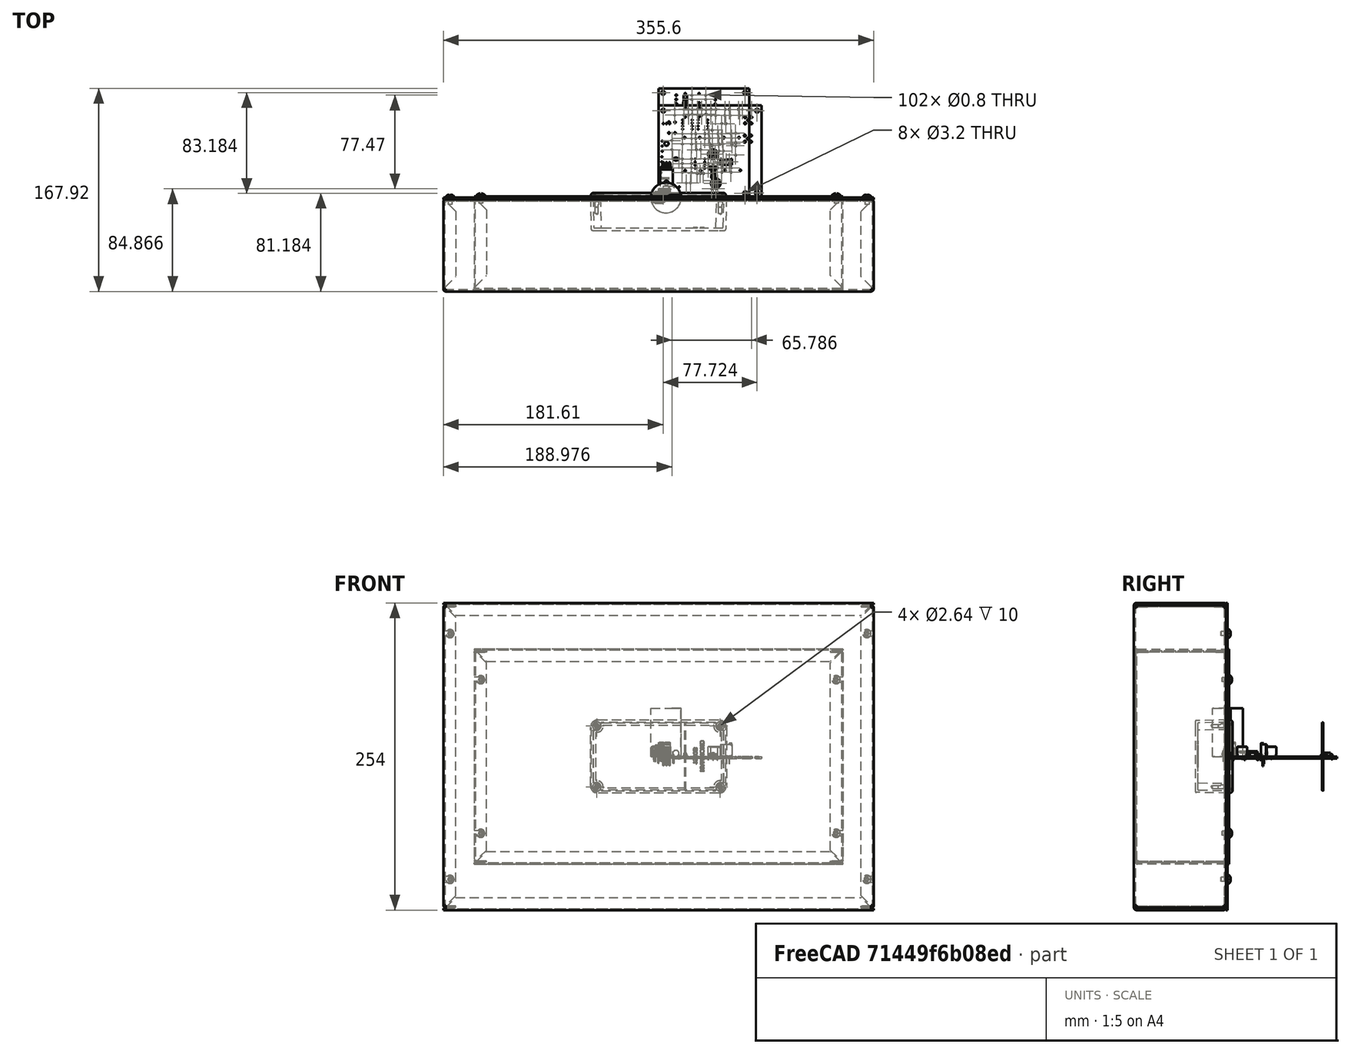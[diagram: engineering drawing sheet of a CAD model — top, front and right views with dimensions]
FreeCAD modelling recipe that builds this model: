
FCSTD DOCUMENT  (FreeCAD 0.20R29603 (Git))
Label: hammond-enclosure
License: All rights reserved
LicenseURL: http://en.wikipedia.org/wiki/All_rights_reserved
objects: Part::Feature×77, App::Link×60, App::Part×20, PartDesign::CoordinateSystem×2, Sketcher::SketchObject×2
note: 81 computed .brp shape members not serialized (recipe doc carries the construction recipe); baked Part::Feature solids carry a one-line shape summary decoded from their .brp

FEATURE [Part::Feature] Part__Feature  label="1444-1273"
  Placement = pos=(0,-76.2,1.8e-14) rot=(0.57735,0.57735,0.57735;4.18879rad)
  shape: bbox 304.8 x 76.2 x 177.8 mm, 114 faces (baked)
FEATURE [Part::Feature] Part__Feature001  label="1434-127"
  shape: bbox 304.8 x 1.016 x 177.8 mm, 26 faces (baked)
FEATURE [Part::Feature] Part__Feature002  label="6-32 (SC18394)"
  Placement = pos=(146.863,-0.508,63.5) rot=(0,0,1;0rad)
  shape: bbox 7.29 x 8.224 x 7.29 mm, 27 faces (baked)
FEATURE [Part::Feature] Part__Feature003  label="6-32 (SC18394)001"
  Placement = pos=(146.863,-0.508,-63.5) rot=(0,0,1;0rad)
  shape: bbox 7.29 x 8.224 x 7.29 mm, 27 faces (baked)
FEATURE [Part::Feature] Part__Feature004  label="6-32 (SC18394)002"
  Placement = pos=(-146.863,-0.508,-63.5) rot=(0,0,1;0rad)
  shape: bbox 7.29 x 8.224 x 7.29 mm, 27 faces (baked)
FEATURE [Part::Feature] Part__Feature005  label="6-32 (SC18394)003"
  Placement = pos=(-146.863,-0.508,63.5) rot=(0,0,1;0rad)
  shape: bbox 7.29 x 8.224 x 7.29 mm, 27 faces (baked)
FEATURE [App::Part] _444_1273  label="1444-1274"
  Group = -> [Part__Feature,Part__Feature001,Part__Feature002,Part__Feature003,Part__Feature004,Part__Feature005]
  Origin = -> Origin
FEATURE [Part::Feature] Part__Feature006  label="1590B BOX"
  Placement = pos=(0,0,0) rot=(-1,0,0;1.5708rad)
  shape: bbox 112.4 x 261 x 60.52 mm, 255 faces (baked)
FEATURE [Part::Feature] Part__Feature007  label="1590B-BS LID"
  Placement = pos=(0,0,0) rot=(0,0.707107,-0.707107;3.14159rad)
  shape: bbox 112.4 x 6.014 x 61.03 mm, 68 faces (baked)
FEATURE [Part::Feature] Part__Feature008  label="SC530 (screw #6-32X 1_2' FH)"
  Placement = pos=(-51.05,1.5362,25.25) rot=(0,1,0;0.650238rad)
  shape: bbox 6.871 x 11.85 x 6.871 mm, 25 faces (baked)
FEATURE [Part::Feature] Part__Feature009  label="SC530 (screw #6-32X 1_2' FH)001"
  Placement = pos=(-51.05,1.5362,-25.25) rot=(0,-1,0;0.529817rad)
  shape: bbox 6.871 x 11.85 x 6.871 mm, 25 faces (baked)
FEATURE [Part::Feature] Part__Feature010  label="SC530 (screw #6-32X 1_2' FH)002"
  Placement = pos=(51.05,1.5362,25.25) rot=(0,0,1;0rad)
  shape: bbox 6.871 x 11.85 x 6.871 mm, 25 faces (baked)
FEATURE [Part::Feature] Part__Feature011  label="SC530 (screw #6-32X 1_2' FH)003"
  Placement = pos=(51.05,1.5362,-25.25) rot=(0,0,1;0rad)
  shape: bbox 6.871 x 11.85 x 6.871 mm, 25 faces (baked)
FEATURE [App::Part] _590B  label="1590B-1"
  Group = -> [Part__Feature006,Part__Feature007,Part__Feature008,Part__Feature009,Part__Feature010,Part__Feature011]
  Origin = -> Origin001
  Placement = pos=(-86,-43,49) rot=(0,0,1;0rad)
FEATURE [Part::Feature] Part__Feature012  label="1590B BOX001"
  Placement = pos=(0,0,0) rot=(-1,0,0;1.5708rad)
  shape: bbox 112.4 x 261 x 60.52 mm, 255 faces (baked)
FEATURE [Part::Feature] Part__Feature013  label="1590B-BS LID001"
  Placement = pos=(0,0,0) rot=(0,0.707107,-0.707107;3.14159rad)
  shape: bbox 112.4 x 6.014 x 61.03 mm, 68 faces (baked)
FEATURE [Part::Feature] Part__Feature014  label="SC530 (screw #6-32X 1_2' FH)004"
  Placement = pos=(-51.05,1.5362,25.25) rot=(0,1,0;0.650238rad)
  shape: bbox 6.871 x 11.85 x 6.871 mm, 25 faces (baked)
FEATURE [Part::Feature] Part__Feature015  label="SC530 (screw #6-32X 1_2' FH)005"
  Placement = pos=(-51.05,1.5362,-25.25) rot=(0,-1,0;0.529817rad)
  shape: bbox 6.871 x 11.85 x 6.871 mm, 25 faces (baked)
FEATURE [Part::Feature] Part__Feature016  label="SC530 (screw #6-32X 1_2' FH)006"
  Placement = pos=(51.05,1.5362,25.25) rot=(0,0,1;0rad)
  shape: bbox 6.871 x 11.85 x 6.871 mm, 25 faces (baked)
FEATURE [Part::Feature] Part__Feature017  label="SC530 (screw #6-32X 1_2' FH)007"
  Placement = pos=(51.05,1.5362,-25.25) rot=(0,0,1;0rad)
  shape: bbox 6.871 x 11.85 x 6.871 mm, 25 faces (baked)
FEATURE [App::Part] _590B001  label="1590B-2"
  Group = -> [Part__Feature012,Part__Feature013,Part__Feature014,Part__Feature015,Part__Feature016,Part__Feature017]
  Origin = -> Origin002
  Placement = pos=(-84,-43,-16) rot=(0,0,1;0rad)
FEATURE [Part::Feature] Part__Feature018  label="1590B BOX002"
  Placement = pos=(0,0,0) rot=(-1,0,0;1.5708rad)
  shape: bbox 112.4 x 261 x 60.52 mm, 255 faces (baked)
FEATURE [Part::Feature] Part__Feature019  label="1590B-BS LID002"
  Placement = pos=(0,0,0) rot=(0,0.707107,-0.707107;3.14159rad)
  shape: bbox 112.4 x 6.014 x 61.03 mm, 68 faces (baked)
FEATURE [Part::Feature] Part__Feature020  label="SC530 (screw #6-32X 1_2' FH)008"
  Placement = pos=(-51.05,1.5362,25.25) rot=(0,1,0;0.650238rad)
  shape: bbox 6.871 x 11.85 x 6.871 mm, 25 faces (baked)
FEATURE [Part::Feature] Part__Feature021  label="SC530 (screw #6-32X 1_2' FH)009"
  Placement = pos=(-51.05,1.5362,-25.25) rot=(0,-1,0;0.529817rad)
  shape: bbox 6.871 x 11.85 x 6.871 mm, 25 faces (baked)
FEATURE [Part::Feature] Part__Feature022  label="SC530 (screw #6-32X 1_2' FH)010"
  Placement = pos=(51.05,1.5362,25.25) rot=(0,0,1;0rad)
  shape: bbox 6.871 x 11.85 x 6.871 mm, 25 faces (baked)
FEATURE [Part::Feature] Part__Feature023  label="SC530 (screw #6-32X 1_2' FH)011"
  Placement = pos=(51.05,1.5362,-25.25) rot=(0,0,1;0rad)
  shape: bbox 6.871 x 11.85 x 6.871 mm, 25 faces (baked)
FEATURE [App::Part] _590B002  label="1590B-3"
  Group = -> [Part__Feature018,Part__Feature019,Part__Feature020,Part__Feature021,Part__Feature022,Part__Feature023]
  Origin = -> Origin003
  Placement = pos=(-85,-9,49) rot=(0,0,1;0rad)
FEATURE [PartDesign::CoordinateSystem] Local_CS_7b02
  AttacherType = Attacher::AttachEngine3D
  MapMode = 2
  Support = -> [X_Axis005]
FEATURE [Part::Feature] Pcb_7b02
  Placement = pos=(-75.946,138.684,0) rot=(0,0,1;0rad)
  shape: bbox 75.18 x 90.42 x 1.6 mm, 56 faces (baked)
FEATURE [Sketcher::SketchObject] PCB_Sketch_7b02
  FullyConstrained = false
  sketch-geometry (4):
    g0: LineSegment StartX=0 StartY=90.424 StartZ=0 EndX=75.184 EndY=90.424 EndZ=0
    g1: LineSegment StartX=75.184 StartY=90.424 StartZ=0 EndX=75.184 EndY=0 EndZ=0
    g2: LineSegment StartX=75.184 StartY=0 StartZ=0 EndX=0 EndY=0 EndZ=0
    g3: LineSegment StartX=0 StartY=0 StartZ=0 EndX=0 EndY=90.424 EndZ=0
  constraints (4):
    c: Coincident(g2,g3)
    c: Coincident(g0,g3)
    c: Coincident(g1,g2)
    c: Coincident(g0,g1)
FEATURE [App::Part] Board_Geoms_7b02
  Group = -> [Pcb_7b02,PCB_Sketch_7b02]
  Origin = -> Origin004
FEATURE [Part::Feature] Part__Feature024  label="part"
  shape: bbox 0.508 x 0.508 x 4.064 mm, 3 faces (baked)
FEATURE [Part::Feature] Part__Feature025  label="part001"
  shape: bbox 0.508 x 0.508 x 4.064 mm, 3 faces (baked)
FEATURE [Part::Feature] Part__Feature026  label="part002"
  shape: bbox 5.994 x 3.506 x 8.509 mm, 6 faces (baked)
FEATURE [App::Part] part  label="C909_part003_af03f52f8d81"
  Group = -> [Part__Feature024,Part__Feature025,Part__Feature026]
  Origin = -> Origin012
  Placement = pos=(39.37,72.644,0) rot=(0,0,-1;1.5708rad)
FEATURE [App::Link] C909_part003_af03f52f8d81_ln_  label="C906_part003_3db3d25175d7"
  LinkPlacement = pos=(27.691,84.808,0) rot=(0,0,-1;1.5708rad)
  LinkedObject = -> part
  Placement = pos=(27.691,84.808,0) rot=(0,0,-1;1.5708rad)
FEATURE [Part::Feature] Part__Feature027  label="SOLID"
  Placement = pos=(0,0,4.2) rot=(0,0,1;0rad)
  shape: bbox 2.75 x 3.75 x 8.15 mm, 17 faces (baked)
FEATURE [Part::Feature] Part__Feature028  label="SOLID001"
  Placement = pos=(0,0,4.2) rot=(0,0,1;0rad)
  shape: bbox 2.75 x 3.75 x 8.15 mm, 17 faces (baked)
FEATURE [Part::Feature] Part__Feature029  label="SOLID002"
  Placement = pos=(0,0,4.2) rot=(0,0,1;0rad)
  shape: bbox 2.75 x 3.75 x 8.15 mm, 17 faces (baked)
FEATURE [Part::Feature] Part__Feature030  label="SOLID003"
  Placement = pos=(0,0,4.2) rot=(0,0,1;0rad)
  shape: bbox 2.9 x 4.5 x 2.65 mm, 46 faces (baked)
FEATURE [Part::Feature] Part__Feature031  label="SOLID004"
  Placement = pos=(0,0,4.2) rot=(0,0,1;0rad)
  shape: bbox 2.9 x 4.5 x 2.65 mm, 46 faces (baked)
FEATURE [Part::Feature] Part__Feature032  label="SOLID005"
  Placement = pos=(0,0,4.2) rot=(0,0,1;0rad)
  shape: bbox 2.9 x 4.5 x 2.65 mm, 46 faces (baked)
FEATURE [Part::Feature] Part__Feature033  label="SOLID006"
  Placement = pos=(0,0,4.2) rot=(0,0,1;0rad)
  shape: bbox 3.139 x 3.139 x 4.6 mm, 17 faces (baked)
FEATURE [Part::Feature] Part__Feature034  label="SOLID007"
  Placement = pos=(0,0,4.2) rot=(0,0,1;0rad)
  shape: bbox 3.139 x 3.139 x 4.6 mm, 17 faces (baked)
FEATURE [Part::Feature] Part__Feature035  label="SOLID008"
  Placement = pos=(0,0,4.2) rot=(0,0,1;0rad)
  shape: bbox 3.139 x 3.139 x 4.6 mm, 17 faces (baked)
FEATURE [Part::Feature] Part__Feature036  label="SOLID009"
  Placement = pos=(0,0,4.2) rot=(0,0,1;0rad)
  shape: bbox 11.5 x 7 x 8.4 mm, 98 faces (baked)
FEATURE [App::Part] _91103110003_1  label="J901_691103110003_1_4d612100a2a6"
  Group = -> [Part__Feature027,Part__Feature028,Part__Feature029,Part__Feature030,Part__Feature031,Part__Feature032,Part__Feature033,Part__Feature034,Part__Feature035,Part__Feature036]
  Origin = -> Origin013
  Placement = pos=(14.732,81.28,0) rot=(0,0,-1;1.5708rad)
FEATURE [App::Link] J901_691103110003_1_4d612100a2a6_ln_  label="J901_691103110003_1_4d612100a2a6[2]"
  LinkPlacement = pos=(14.732,81.28,4) rot=(0,0,-1;1.5708rad)
  LinkedObject = -> _91103110003_1
  Placement = pos=(14.732,81.28,4) rot=(0,0,-1;1.5708rad)
FEATURE [Part::Feature] Shape  label="D901_D_DO-41_SOD81_P7.62mm_Horizontal_0f7420698e15"
  Placement = pos=(22.098,78.486,0) rot=(0,0,1;1.5708rad)
  shape: bbox 2.72 x 8.618 x 5.71 mm, 15 faces (baked)
FEATURE [Part::Feature] Shape001  label="D901_SOD57  BYT62-BY203_6-563-5006-5-4_0f7420698e15[2]"
  Placement = pos=(22.098,78.486,0) rot=(0,0,1;1.5708rad)
  shape: bbox 4.349 x 4.349 x 56.22 mm, 10 faces (baked)
FEATURE [App::Link] D901_D_DO_41_SOD81_P7_62mm_Horizontal_0f7420698e15_ln_  label="D904_D_DO-41_SOD81_P7.62mm_Horizontal_3765f3f7798b"
  LinkPlacement = pos=(33.528,66.802,0) rot=(0,0,1;1.5708rad)
  LinkedObject = -> Shape
  Placement = pos=(33.528,66.802,0) rot=(0,0,1;1.5708rad)
FEATURE [Part::Feature] Part__Feature037  label="part003"
  shape: bbox 1.016 x 1.016 x 5.588 mm, 3 faces (baked)
FEATURE [Part::Feature] Part__Feature038  label="part004"
  shape: bbox 1.016 x 1.016 x 5.588 mm, 3 faces (baked)
FEATURE [Part::Feature] Part__Feature039  label="part005"
  shape: bbox 24.99 x 24.99 x 39.75 mm, 3 faces (baked)
FEATURE [Part::Feature] Part__Feature040  label="part006"
  shape: bbox 10.02 x 4.878 x 31.83 mm, 8 faces (baked)
FEATURE [App::Part] part001  label="C911_part007_10cb9a3285f4"
  Group = -> [Part__Feature037,Part__Feature038,Part__Feature039,Part__Feature040]
  Origin = -> Origin014
  Placement = pos=(54.102,49.784,0) rot=(0,0,1;0rad)
FEATURE [App::Link] C911_part007_10cb9a3285f4_ln_  label="C902_part007_474a571f78e2"
  LinkPlacement = pos=(21.59,49.784,0) rot=(0,0,1;0rad)
  LinkedObject = -> part001
  Placement = pos=(21.59,49.784,0) rot=(0,0,1;0rad)
FEATURE [Part::Feature] Shape002  label="R902_R_Axial_DIN0309_L90mm_D32mm_P1270mm_Horizontal_656395d6a1e4"
  Placement = pos=(45.212,14.224,0) rot=(0,0,1;1.5708rad)
  shape: bbox 3.464 x 13.63 x 6.332 mm, 17 faces (baked)
FEATURE [App::Link] C911_part007_10cb9a3285f4_ln_001  label="C910_part007_5ecea69d9437"
  LinkPlacement = pos=(55.118,22.606,0) rot=(0,0,1;0rad)
  LinkedObject = -> part001
  Placement = pos=(55.118,22.606,0) rot=(0,0,1;0rad)
FEATURE [App::Link] C909_part003_af03f52f8d81_ln_001  label="C907_part007_ae6a843ea56a"
  LinkPlacement = pos=(27.945,72.616,0) rot=(0,0,-1;1.5708rad)
  LinkedObject = -> part
  Placement = pos=(27.945,72.616,0) rot=(0,0,-1;1.5708rad)
FEATURE [Part::Feature] Shape003  label="C904_CP_Radial_D80mm_P350mm_be9362f17a2f"
  Placement = pos=(43.2449,36.068,0) rot=(0,0,1;0rad)
  shape: bbox 9.886 x 10.23 x 10 mm, 54 faces (baked)
FEATURE [App::Link] D901_D_DO_41_SOD81_P7_62mm_Horizontal_0f7420698e15_ln_001  label="D902_D_DO-41_SOD81_P7.62mm_Horizontal_acca8f042afe"
  LinkPlacement = pos=(22.098,66.802,0) rot=(0,0,1;1.5708rad)
  LinkedObject = -> Shape
  Placement = pos=(22.098,66.802,0) rot=(0,0,1;1.5708rad)
FEATURE [App::Link] C904_CP_Radial_D80mm_P350mm_be9362f17a2f_ln_  label="C905_CP_Radial_D80mm_P350mm_1a9500cd5eb0"
  LinkPlacement = pos=(44.0069,7.366,0) rot=(0,0,1;0rad)
  LinkedObject = -> Shape003
  Placement = pos=(44.0069,7.366,0) rot=(0,0,1;0rad)
FEATURE [App::Link] R902_R_Axial_DIN0309_L90mm_D32mm_P1270mm_Horizontal_656395d6a1e4_ln_  label="R901_R_Axial_DIN0309_L90mm_D32mm_P1270mm_Horizontal_c8b94c641cc7"
  LinkPlacement = pos=(44.45,43.18,0) rot=(0,0,1;1.5708rad)
  LinkedObject = -> Shape002
  Placement = pos=(44.45,43.18,0) rot=(0,0,1;1.5708rad)
FEATURE [Part::Feature] Shape004  label="U902_TO-220-3_Horizontal_TabUp_336c31f2f8c4"
  Placement = pos=(4.064,28.956,0) rot=(0,0,1;0rad)
  shape: bbox 10.25 x 19.74 x 12.59 mm, 80 faces (baked)
FEATURE [App::Link] U902_TO_220_3_Horizontal_TabUp_336c31f2f8c4_ln_  label="U902_TO-220-3_Horizontal_TabUp_336c31f2f8c4[2]"
  LinkPlacement = pos=(4.064,28.956,0) rot=(0,0,1;0rad)
  LinkedObject = -> Shape004
  Placement = pos=(4.064,28.956,0) rot=(0,0,1;0rad)
FEATURE [App::Link] J901_691103110003_1_4d612100a2a6_ln_001  label="J902_691103110003_1_2f685726ded9"
  LinkPlacement = pos=(46.99,81.026,0) rot=(0,0,1;1.5708rad)
  LinkedObject = -> _91103110003_1
  Placement = pos=(46.99,81.026,0) rot=(0,0,1;1.5708rad)
FEATURE [App::Link] J901_691103110003_1_4d612100a2a6_ln_002  label="J902_691103110003_1_2f685726ded9[2]"
  LinkPlacement = pos=(46.99,81.026,4) rot=(0,0,1;1.5708rad)
  LinkedObject = -> _91103110003_1
  Placement = pos=(46.99,81.026,4) rot=(0,0,1;1.5708rad)
FEATURE [App::Link] D901_D_DO_41_SOD81_P7_62mm_Horizontal_0f7420698e15_ln_002  label="D903_D_DO-41_SOD81_P7.62mm_Horizontal_fd54faef2eec"
  LinkPlacement = pos=(33.528,78.486,0) rot=(0,0,1;1.5708rad)
  LinkedObject = -> Shape
  Placement = pos=(33.528,78.486,0) rot=(0,0,1;1.5708rad)
FEATURE [App::Link] U902_TO_220_3_Horizontal_TabUp_336c31f2f8c4_ln_001  label="U901_TO-220-3_Horizontal_TabUp_2bf8607644b3"
  LinkPlacement = pos=(4.064,61.3,0) rot=(0,0,1;0rad)
  LinkedObject = -> Shape004
  Placement = pos=(4.064,61.3,0) rot=(0,0,1;0rad)
FEATURE [App::Link] U902_TO_220_3_Horizontal_TabUp_336c31f2f8c4_ln_002  label="U901_TO-220-3_Horizontal_TabUp_2bf8607644b3[2]"
  LinkPlacement = pos=(4.064,61.3,0) rot=(0,0,1;0rad)
  LinkedObject = -> Shape004
  Placement = pos=(4.064,61.3,0) rot=(0,0,1;0rad)
FEATURE [App::Link] C909_part003_af03f52f8d81_ln_002  label="C908_part007_641f8a291a63"
  LinkPlacement = pos=(39.121,84.836,0) rot=(0,0,-1;1.5708rad)
  LinkedObject = -> part
  Placement = pos=(39.121,84.836,0) rot=(0,0,-1;1.5708rad)
FEATURE [App::Link] C911_part007_10cb9a3285f4_ln_002  label="C903_part007_61d36386d3d2"
  LinkPlacement = pos=(22.1411,22.352,0) rot=(0,0,1;0rad)
  LinkedObject = -> part001
  Placement = pos=(22.1411,22.352,0) rot=(0,0,1;0rad)
FEATURE [App::Part] Top_7b02
  Group = -> [part,C909_part003_af03f52f8d81_ln_,_91103110003_1,J901_691103110003_1_4d612100a2a6_ln_,Shape,Shape001,D901_D_DO_41_SOD81_P7_62mm_Horizontal_0f7420698e15_ln_,part001,C911_part007_10cb9a3285f4_ln_,Shape002,C911_part007_10cb9a3285f4_ln_001,C909_part003_af03f52f8d81_ln_001,Shape003,D901_D_DO_41_SOD81_P7_62mm_Horizontal_0f7420698e15_ln_001,C904_CP_Radial_D80mm_P350mm_be9362f17a2f_ln_,+10 more]
  Origin = -> Origin007
FEATURE [App::Part] Step_Models_7b02
  Group = -> [Top_7b02]
  Origin = -> Origin006
FEATURE [App::Part] Board_7b02  label="15v-supply"
  Group = -> [Local_CS_7b02,Board_Geoms_7b02,Step_Models_7b02]
  Origin = -> Origin005
  Placement = pos=(62,-65,-77) rot=(0.57735,0.57735,0.57735;4.18879rad)
FEATURE [PartDesign::CoordinateSystem] Local_CS_758f
  AttacherType = Attacher::AttachEngine3D
  MapMode = 2
  Support = -> [X_Axis016]
FEATURE [Part::Feature] Pcb_758f
  Placement = pos=(-97.028,138.43,0) rot=(0,0,1;0rad)
  shape: bbox 85.34 x 76.45 x 1.6 mm, 146 faces (baked)
FEATURE [Sketcher::SketchObject] PCB_Sketch_758f
  FullyConstrained = false
  sketch-geometry (4):
    g0: LineSegment StartX=0 StartY=76.454 StartZ=0 EndX=85.344 EndY=76.454 EndZ=0
    g1: LineSegment StartX=85.344 StartY=76.454 StartZ=0 EndX=85.344 EndY=0 EndZ=0
    g2: LineSegment StartX=85.344 StartY=0 StartZ=0 EndX=0 EndY=0 EndZ=0
    g3: LineSegment StartX=0 StartY=0 StartZ=0 EndX=0 EndY=76.454 EndZ=0
  constraints (4):
    c: Coincident(g2,g3)
    c: Coincident(g0,g3)
    c: Coincident(g1,g2)
    c: Coincident(g0,g1)
FEATURE [App::Part] Board_Geoms_758f
  Group = -> [Pcb_758f,PCB_Sketch_758f]
  Origin = -> Origin015
FEATURE [Part::Feature] Shape005  label="R426_R_Axial_DIN0207_L63mm_D25mm_P762mm_Horizontal_96b38c16849e"
  Placement = pos=(48.768,24.638,0) rot=(0,0,1;3.14159rad)
  shape: bbox 8.418 x 2.706 x 5.603 mm, 15 faces (baked)
FEATURE [Part::Feature] Part__Feature041  label="D_DO-35_SOD27_P7.62mm_Horizontal"
  shape: bbox 8.244 x 0.5 x 4.312 mm, 7 faces (baked)
FEATURE [Part::Feature] Part__Feature042  label="D_DO-35_SOD27_P7.62mm_Horizontal001"
  shape: bbox 4 x 2.165 x 2.165 mm, 9 faces (baked)
FEATURE [App::Part] D_DO_35_SOD27_P7_62mm_Horizontal  label="D401_D_DO-35_SOD27_P7.62mm_Horizontal002_a58dadb01c92"
  Group = -> [Part__Feature041,Part__Feature042]
  Origin = -> Origin023
  Placement = pos=(24.638,73.152,0) rot=(0,0,1;0rad)
FEATURE [App::Link] R426_R_Axial_DIN0207_L63mm_D25mm_P762mm_Horizontal_96b38c16849e_ln_  label="R411_R_Axial_DIN0207_L63mm_D25mm_P762mm_Horizontal_dd1791483003"
  LinkPlacement = pos=(13.462,68.326,0) rot=(0,0,1;0rad)
  LinkedObject = -> Shape005
  Placement = pos=(13.462,68.326,0) rot=(0,0,1;0rad)
FEATURE [Part::Feature] Shape006  label="C405_CP_Radial_D80mm_P350mm_98bf3544fc31"
  Placement = pos=(45.5913,11.938,0) rot=(0,0,1;0rad)
  shape: bbox 9.886 x 10.23 x 10 mm, 54 faces (baked)
FEATURE [App::Link] R426_R_Axial_DIN0207_L63mm_D25mm_P762mm_Horizontal_96b38c16849e_ln_001  label="R425_R_Axial_DIN0207_L63mm_D25mm_P762mm_Horizontal_9357a432a3ac"
  LinkPlacement = pos=(52.324,24.638,0) rot=(0,0,1;0rad)
  LinkedObject = -> Shape005
  Placement = pos=(52.324,24.638,0) rot=(0,0,1;0rad)
FEATURE [App::Link] R426_R_Axial_DIN0207_L63mm_D25mm_P762mm_Horizontal_96b38c16849e_ln_002  label="R417_R_Axial_DIN0207_L63mm_D25mm_P762mm_Horizontal_e48147e24a71"
  LinkPlacement = pos=(19.558,20.828,0) rot=(0,0,1;0rad)
  LinkedObject = -> Shape005
  Placement = pos=(19.558,20.828,0) rot=(0,0,1;0rad)
FEATURE [App::Link] R426_R_Axial_DIN0207_L63mm_D25mm_P762mm_Horizontal_96b38c16849e_ln_003  label="R412_R_Axial_DIN0207_L63mm_D25mm_P762mm_Horizontal_5f7197d756d8"
  LinkPlacement = pos=(24.892,68.326,0) rot=(0,0,1;0rad)
  LinkedObject = -> Shape005
  Placement = pos=(24.892,68.326,0) rot=(0,0,1;0rad)
FEATURE [App::Link] R426_R_Axial_DIN0207_L63mm_D25mm_P762mm_Horizontal_96b38c16849e_ln_004  label="R401_R_Axial_DIN0207_L63mm_D25mm_P762mm_Horizontal_f955ca19a62c"
  LinkPlacement = pos=(11.176,47.244,0) rot=(0,0,-1;1.5708rad)
  LinkedObject = -> Shape005
  Placement = pos=(11.176,47.244,0) rot=(0,0,-1;1.5708rad)
FEATURE [Part::Feature] Shape007  label="C401_C_Disc_D50mm_W25mm_P500mm_d1dd1edc5a97"
  Placement = pos=(11.938,32.004,0) rot=(0,0,1;0rad)
  shape: bbox 5.5 x 2.5 x 7.1 mm, 10 faces (baked)
FEATURE [App::Link] D401_D_DO_35_SOD27_P7_62mm_Horizontal002_a58dadb01c92_ln_  label="D402_D_DO-35_SOD27_P7.62mm_Horizontal002_911bd0e35fae"
  LinkPlacement = pos=(43.434,73.152,0) rot=(0,0,1;3.14159rad)
  LinkedObject = -> D_DO_35_SOD27_P7_62mm_Horizontal
  Placement = pos=(43.434,73.152,0) rot=(0,0,1;3.14159rad)
FEATURE [App::Link] R426_R_Axial_DIN0207_L63mm_D25mm_P762mm_Horizontal_96b38c16849e_ln_005  label="R415_R_Axial_DIN0207_L63mm_D25mm_P762mm_Horizontal_2c18ec95c2a3"
  LinkPlacement = pos=(58.42,72.898,0) rot=(0,0,1;0rad)
  LinkedObject = -> Shape005
  Placement = pos=(58.42,72.898,0) rot=(0,0,1;0rad)
FEATURE [App::Link] C405_CP_Radial_D80mm_P350mm_98bf3544fc31_ln_  label="C403_CP_Radial_D80mm_P350mm_8a6e5d1b3050"
  LinkPlacement = pos=(34.9267,39.624,0) rot=(0,0,1;3.14159rad)
  LinkedObject = -> Shape006
  Placement = pos=(34.9267,39.624,0) rot=(0,0,1;3.14159rad)
FEATURE [App::Link] R426_R_Axial_DIN0207_L63mm_D25mm_P762mm_Horizontal_96b38c16849e_ln_006  label="R419_R_Axial_DIN0207_L63mm_D25mm_P762mm_Horizontal_3cb2f076483c"
  LinkPlacement = pos=(19.558,32.004,0) rot=(0,0,1;0rad)
  LinkedObject = -> Shape005
  Placement = pos=(19.558,32.004,0) rot=(0,0,1;0rad)
FEATURE [Part::Feature] Part__Feature043  label="OPA347PA"
  Placement = pos=(0.013,0.081953,-0.39) rot=(1,0,0;1.5708rad)
  shape: bbox 0.762 x 1.461 x 6.731 mm, 18 faces (baked)
FEATURE [Part::Feature] Part__Feature044  label="OPA347PA001"
  Placement = pos=(0.013,0.081953,-0.39) rot=(1,0,0;1.5708rad)
  shape: bbox 0.762 x 0.9589 x 6.731 mm, 15 faces (baked)
FEATURE [Part::Feature] Part__Feature045  label="OPA347PA002"
  Placement = pos=(0.013,0.081953,-0.39) rot=(1,0,0;1.5708rad)
  shape: bbox 0.762 x 1.461 x 6.731 mm, 18 faces (baked)
FEATURE [Part::Feature] Part__Feature046  label="OPA347PA003"
  Placement = pos=(0.013,0.081953,-0.39) rot=(1,0,0;1.5708rad)
  shape: bbox 0.762 x 0.9589 x 6.731 mm, 15 faces (baked)
FEATURE [Part::Feature] Part__Feature047  label="OPA347PA004"
  Placement = pos=(0.013,0.081953,-0.39) rot=(1,0,0;1.5708rad)
  shape: bbox 0.762 x 1.461 x 6.731 mm, 18 faces (baked)
FEATURE [Part::Feature] Part__Feature048  label="OPA347PA005"
  Placement = pos=(0.013,0.081953,-0.39) rot=(1,0,0;1.5708rad)
  shape: bbox 0.762 x 0.9589 x 6.731 mm, 15 faces (baked)
FEATURE [Part::Feature] Part__Feature049  label="OPA347PA006"
  Placement = pos=(0.013,0.081953,-0.39) rot=(1,0,0;1.5708rad)
  shape: bbox 0.762 x 1.461 x 6.731 mm, 18 faces (baked)
FEATURE [Part::Feature] Part__Feature050  label="OPA347PA007"
  Placement = pos=(0.013,0.081953,-0.39) rot=(1,0,0;1.5708rad)
  shape: bbox 0.762 x 0.9589 x 6.731 mm, 15 faces (baked)
FEATURE [Part::Feature] Part__Feature051  label="OPA347PA008"
  Placement = pos=(0.013,0.081953,-0.39) rot=(1,0,0;1.5708rad)
  shape: bbox 6.35 x 9.589 x 4.572 mm, 17 faces (baked)
FEATURE [Part::Feature] Part__Feature052  label="OPA347PA009"
  Placement = pos=(0.013,0.081953,-0.39) rot=(1,0,0;1.5708rad)
  shape: bbox 0.6132 x 0.6132 x 0.508 mm, 4 faces (baked)
FEATURE [App::Part] OPA347PA010  label="U403_OPA347PA010_c6fd33d6b5eb"
  Group = -> [Part__Feature043,Part__Feature044,Part__Feature045,Part__Feature046,Part__Feature047,Part__Feature048,Part__Feature049,Part__Feature050,Part__Feature051,Part__Feature052]
  Origin = -> Origin024
  Placement = pos=(34.29,28.194,0) rot=(0,0,1;0rad)
FEATURE [App::Link] D401_D_DO_35_SOD27_P7_62mm_Horizontal002_a58dadb01c92_ln_001  label="D405_D_DO-35_SOD27_P7.62mm_Horizontal002_9d44dfe04af6"
  LinkPlacement = pos=(42.418,44.45,0) rot=(0,0,1;0rad)
  LinkedObject = -> D_DO_35_SOD27_P7_62mm_Horizontal
  Placement = pos=(42.418,44.45,0) rot=(0,0,1;0rad)
FEATURE [App::Link] R426_R_Axial_DIN0207_L63mm_D25mm_P762mm_Horizontal_96b38c16849e_ln_007  label="R416_R_Axial_DIN0207_L63mm_D25mm_P762mm_Horizontal_a3ec67ffc637"
  LinkPlacement = pos=(69.342,72.898,0) rot=(0,0,1;0rad)
  LinkedObject = -> Shape005
  Placement = pos=(69.342,72.898,0) rot=(0,0,1;0rad)
FEATURE [App::Link] C405_CP_Radial_D80mm_P350mm_98bf3544fc31_ln_001  label="C406_CP_Radial_D80mm_P350mm_5d0f856a23b9"
  LinkPlacement = pos=(55.7547,61.214,0) rot=(0,0,1;3.14159rad)
  LinkedObject = -> Shape006
  Placement = pos=(55.7547,61.214,0) rot=(0,0,1;3.14159rad)
FEATURE [App::Link] R426_R_Axial_DIN0207_L63mm_D25mm_P762mm_Horizontal_96b38c16849e_ln_008  label="R414_R_Axial_DIN0207_L63mm_D25mm_P762mm_Horizontal_e16ba095c79a"
  LinkPlacement = pos=(47.498,72.898,0) rot=(0,0,1;0rad)
  LinkedObject = -> Shape005
  Placement = pos=(47.498,72.898,0) rot=(0,0,1;0rad)
FEATURE [App::Link] R426_R_Axial_DIN0207_L63mm_D25mm_P762mm_Horizontal_96b38c16849e_ln_009  label="R403_R_Axial_DIN0207_L63mm_D25mm_P762mm_Horizontal_d589118723d7"
  LinkPlacement = pos=(38.354,49.022,0) rot=(0,0,1;3.14159rad)
  LinkedObject = -> Shape005
  Placement = pos=(38.354,49.022,0) rot=(0,0,1;3.14159rad)
FEATURE [Part::Feature] Part__Feature053  label="73391-0060"
  Placement = pos=(0,9e-16,-9e-16) rot=(1,0,0;1.5708rad)
  shape: bbox 4.16 x 4.16 x 0.3 mm, 6 faces (baked)
FEATURE [Part::Feature] Part__Feature054  label="73391-0061"
  Placement = pos=(0,9e-16,-9e-16) rot=(1,0,0;1.5708rad)
  shape: bbox 1.254 x 0.5508 x 2.67 mm, 9 faces (baked)
FEATURE [Part::Feature] Part__Feature055  label="73391-0062"
  Placement = pos=(0,9e-16,-9e-16) rot=(1,0,0;1.5708rad)
  shape: bbox 1.254 x 0.5508 x 2.67 mm, 9 faces (baked)
FEATURE [Part::Feature] Part__Feature056  label="73391-0063"
  Placement = pos=(0,9e-16,-9e-16) rot=(1,0,0;1.5708rad)
  shape: bbox 6.358 x 7.341 x 13.63 mm, 83 faces (baked)
FEATURE [Part::Feature] Part__Feature057  label="73391-0064"
  Placement = pos=(0,9e-16,-9e-16) rot=(1,0,0;1.5708rad)
  shape: bbox 3.46 x 3.46 x 2.77 mm, 7 faces (baked)
FEATURE [App::Part] _3391_0065  label="J9_73391-0065_751de25d1e29"
  Group = -> [Part__Feature053,Part__Feature054,Part__Feature055,Part__Feature056,Part__Feature057]
  Origin = -> Origin025
  Placement = pos=(74.168,64.008,0) rot=(0,0,1;0rad)
FEATURE [App::Link] J9_73391_0065_751de25d1e29_ln_  label="J9_73391-0065_751de25d1e29[2]"
  LinkPlacement = pos=(74.168,64.008,0) rot=(0,0,1;0rad)
  LinkedObject = -> _3391_0065
  Placement = pos=(74.168,64.008,0) rot=(0,0,1;0rad)
FEATURE [App::Link] R426_R_Axial_DIN0207_L63mm_D25mm_P762mm_Horizontal_96b38c16849e_ln_010  label="R413_R_Axial_DIN0207_L63mm_D25mm_P762mm_Horizontal_7eeb8a3caef1"
  LinkPlacement = pos=(35.814,68.326,0) rot=(0,0,1;0rad)
  LinkedObject = -> Shape005
  Placement = pos=(35.814,68.326,0) rot=(0,0,1;0rad)
FEATURE [App::Link] R426_R_Axial_DIN0207_L63mm_D25mm_P762mm_Horizontal_96b38c16849e_ln_011  label="R422_R_Axial_DIN0207_L63mm_D25mm_P762mm_Horizontal_5ecc24362076"
  LinkPlacement = pos=(19.558,24.638,0) rot=(0,0,1;0rad)
  LinkedObject = -> Shape005
  Placement = pos=(19.558,24.638,0) rot=(0,0,1;0rad)
FEATURE [App::Link] R426_R_Axial_DIN0207_L63mm_D25mm_P762mm_Horizontal_96b38c16849e_ln_012  label="R406_R_Axial_DIN0207_L63mm_D25mm_P762mm_Horizontal_069660b694ff"
  LinkPlacement = pos=(19.812,52.832,0) rot=(0,0,1;0rad)
  LinkedObject = -> Shape005
  Placement = pos=(19.812,52.832,0) rot=(0,0,1;0rad)
FEATURE [App::Link] D401_D_DO_35_SOD27_P7_62mm_Horizontal002_a58dadb01c92_ln_002  label="D408_D_DO-35_SOD27_P7.62mm_Horizontal002_46fe6fc0bc71"
  LinkPlacement = pos=(59.436,68.072,0) rot=(0,0,1;0rad)
  LinkedObject = -> D_DO_35_SOD27_P7_62mm_Horizontal
  Placement = pos=(59.436,68.072,0) rot=(0,0,1;0rad)
FEATURE [App::Link] R426_R_Axial_DIN0207_L63mm_D25mm_P762mm_Horizontal_96b38c16849e_ln_013  label="R427_R_Axial_DIN0207_L63mm_D25mm_P762mm_Horizontal_7b5043e7ec34"
  LinkPlacement = pos=(52.324,21.082,0) rot=(0,0,1;0rad)
  LinkedObject = -> Shape005
  Placement = pos=(52.324,21.082,0) rot=(0,0,1;0rad)
FEATURE [Part::Feature] Shape008  label="R424_Potentiometer_Bourns_3296W_Vertical_5014a80db3f9"
  Placement = pos=(58.684,29.718,0) rot=(0,0,1;0rad)
  shape: bbox 9.53 x 4.83 x 17.07 mm, 32 faces (baked)
FEATURE [App::Link] R426_R_Axial_DIN0207_L63mm_D25mm_P762mm_Horizontal_96b38c16849e_ln_014  label="R421_R_Axial_DIN0207_L63mm_D25mm_P762mm_Horizontal_8707e0924818"
  LinkPlacement = pos=(48.768,32.258,0) rot=(0,0,1;3.14159rad)
  LinkedObject = -> Shape005
  Placement = pos=(48.768,32.258,0) rot=(0,0,1;3.14159rad)
FEATURE [App::Link] R426_R_Axial_DIN0207_L63mm_D25mm_P762mm_Horizontal_96b38c16849e_ln_015  label="R409_R_Axial_DIN0207_L63mm_D25mm_P762mm_Horizontal_5f0248fd6b37"
  LinkPlacement = pos=(52.324,52.832,0) rot=(0,0,1;0rad)
  LinkedObject = -> Shape005
  Placement = pos=(52.324,52.832,0) rot=(0,0,1;0rad)
FEATURE [App::Link] R426_R_Axial_DIN0207_L63mm_D25mm_P762mm_Horizontal_96b38c16849e_ln_016  label="R428_R_Axial_DIN0207_L63mm_D25mm_P762mm_Horizontal_dfc8f80ca371"
  LinkPlacement = pos=(63.754,35.306,0) rot=(0,0,1;1.5708rad)
  LinkedObject = -> Shape005
  Placement = pos=(63.754,35.306,0) rot=(0,0,1;1.5708rad)
FEATURE [App::Link] R426_R_Axial_DIN0207_L63mm_D25mm_P762mm_Horizontal_96b38c16849e_ln_017  label="R407_R_Axial_DIN0207_L63mm_D25mm_P762mm_Horizontal_5106d6ccafbb"
  LinkPlacement = pos=(30.734,52.832,0) rot=(0,0,1;0rad)
  LinkedObject = -> Shape005
  Placement = pos=(30.734,52.832,0) rot=(0,0,1;0rad)
FEATURE [App::Link] D401_D_DO_35_SOD27_P7_62mm_Horizontal002_a58dadb01c92_ln_003  label="D406_D_DO-35_SOD27_P7.62mm_Horizontal002_cf8cdba62340"
  LinkPlacement = pos=(60.706,44.45,0) rot=(0,0,1;3.14159rad)
  LinkedObject = -> D_DO_35_SOD27_P7_62mm_Horizontal
  Placement = pos=(60.706,44.45,0) rot=(0,0,1;3.14159rad)
FEATURE [App::Link] J9_73391_0065_751de25d1e29_ln_001  label="J8_73391-0065_6ead0989832a"
  LinkPlacement = pos=(73.914,48.768,0) rot=(0,0,1;0rad)
  LinkedObject = -> _3391_0065
  Placement = pos=(73.914,48.768,0) rot=(0,0,1;0rad)
FEATURE [App::Link] R426_R_Axial_DIN0207_L63mm_D25mm_P762mm_Horizontal_96b38c16849e_ln_018  label="R405_R_Axial_DIN0207_L63mm_D25mm_P762mm_Horizontal_71255379b79a"
  LinkPlacement = pos=(13.462,72.898,0) rot=(0,0,1;0rad)
  LinkedObject = -> Shape005
  Placement = pos=(13.462,72.898,0) rot=(0,0,1;0rad)
FEATURE [App::Link] U403_OPA347PA010_c6fd33d6b5eb_ln_  label="U401_OPA347PA010_2ab8ee650e3a"
  LinkPlacement = pos=(23.97,60.452,0) rot=(0,0,1;0rad)
  LinkedObject = -> OPA347PA010
  Placement = pos=(23.97,60.452,0) rot=(0,0,1;0rad)
FEATURE [App::Link] U403_OPA347PA010_c6fd33d6b5eb_ln_001  label="U401_OPA347PA010_2ab8ee650e3a[2]"
  LinkPlacement = pos=(23.97,60.452,0) rot=(0,0,1;0rad)
  LinkedObject = -> OPA347PA010
  Placement = pos=(23.97,60.452,0) rot=(0,0,1;0rad)
FEATURE [App::Link] R426_R_Axial_DIN0207_L63mm_D25mm_P762mm_Horizontal_96b38c16849e_ln_019  label="R423_R_Axial_DIN0207_L63mm_D25mm_P762mm_Horizontal_fe47b2319611"
  LinkPlacement = pos=(48.768,28.448,0) rot=(0,0,1;3.14159rad)
  LinkedObject = -> Shape005
  Placement = pos=(48.768,28.448,0) rot=(0,0,1;3.14159rad)
FEATURE [Part::Feature] Part__Feature058  label="SOLID010"
  shape: bbox 5.001 x 7.774 x 15.1 mm, 102 faces (baked)
FEATURE [Part::Feature] Part__Feature059  label="SOLID011"
  shape: bbox 5.001 x 7.774 x 15.1 mm, 102 faces (baked)
FEATURE [App::Part] _91137710002_1  label="J404_691137710002_1_aa849ba69819"
  Group = -> [Part__Feature058,Part__Feature059]
  Origin = -> Origin026
  Placement = pos=(16.176,66.484,0) rot=(0,0,1;3.14159rad)
FEATURE [App::Link] C405_CP_Radial_D80mm_P350mm_98bf3544fc31_ln_002  label="C404_CP_Radial_D80mm_P350mm_9f53755e8169"
  LinkPlacement = pos=(22.9853,12.192,0) rot=(0,0,1;0rad)
  LinkedObject = -> Shape006
  Placement = pos=(22.9853,12.192,0) rot=(0,0,1;0rad)
FEATURE [App::Link] D401_D_DO_35_SOD27_P7_62mm_Horizontal002_a58dadb01c92_ln_004  label="D403_D_DO-35_SOD27_P7.62mm_Horizontal002_2c64fccd57f6"
  LinkPlacement = pos=(52.832,49.276,0) rot=(0,0,1;0rad)
  LinkedObject = -> D_DO_35_SOD27_P7_62mm_Horizontal
  Placement = pos=(52.832,49.276,0) rot=(0,0,1;0rad)
FEATURE [App::Link] R426_R_Axial_DIN0207_L63mm_D25mm_P762mm_Horizontal_96b38c16849e_ln_020  label="R408_R_Axial_DIN0207_L63mm_D25mm_P762mm_Horizontal_61fd169c9d1a"
  LinkPlacement = pos=(49.022,52.832,0) rot=(0,0,1;3.14159rad)
  LinkedObject = -> Shape005
  Placement = pos=(49.022,52.832,0) rot=(0,0,1;3.14159rad)
FEATURE [App::Link] J404_691137710002_1_aa849ba69819_ln_  label="J402_691137710002_1_e33a29fe56de"
  LinkPlacement = pos=(6.176,49.594,0) rot=(0,0,1;0rad)
  LinkedObject = -> _91137710002_1
  Placement = pos=(6.176,49.594,0) rot=(0,0,1;0rad)
FEATURE [App::Link] R426_R_Axial_DIN0207_L63mm_D25mm_P762mm_Horizontal_96b38c16849e_ln_021  label="R410_R_Axial_DIN0207_L63mm_D25mm_P762mm_Horizontal_3c69a267c242"
  LinkPlacement = pos=(63.754,53.34,0) rot=(0,0,-1;1.5708rad)
  LinkedObject = -> Shape005
  Placement = pos=(63.754,53.34,0) rot=(0,0,-1;1.5708rad)
FEATURE [App::Link] R426_R_Axial_DIN0207_L63mm_D25mm_P762mm_Horizontal_96b38c16849e_ln_022  label="R404_R_Axial_DIN0207_L63mm_D25mm_P762mm_Horizontal_fed7218cdfd8"
  LinkPlacement = pos=(19.812,44.45,0) rot=(0,0,1;0rad)
  LinkedObject = -> Shape005
  Placement = pos=(19.812,44.45,0) rot=(0,0,1;0rad)
FEATURE [App::Link] D401_D_DO_35_SOD27_P7_62mm_Horizontal002_a58dadb01c92_ln_005  label="D404_D_DO-35_SOD27_P7.62mm_Horizontal002_1b29f77ed16f"
  LinkPlacement = pos=(49.784,49.276,0) rot=(0,0,1;3.14159rad)
  LinkedObject = -> D_DO_35_SOD27_P7_62mm_Horizontal
  Placement = pos=(49.784,49.276,0) rot=(0,0,1;3.14159rad)
FEATURE [App::Link] C405_CP_Radial_D80mm_P350mm_98bf3544fc31_ln_003  label="C402_CP_Radial_D80mm_P350mm_13afafdb752a"
  LinkPlacement = pos=(53.538,38.608,0) rot=(0,0,1;3.14159rad)
  LinkedObject = -> Shape006
  Placement = pos=(53.538,38.608,0) rot=(0,0,1;3.14159rad)
FEATURE [App::Link] R426_R_Axial_DIN0207_L63mm_D25mm_P762mm_Horizontal_96b38c16849e_ln_023  label="R429_R_Axial_DIN0207_L63mm_D25mm_P762mm_Horizontal_513325376d6c"
  LinkPlacement = pos=(47.244,68.072,0) rot=(0,0,1;0rad)
  LinkedObject = -> Shape005
  Placement = pos=(47.244,68.072,0) rot=(0,0,1;0rad)
FEATURE [App::Link] R426_R_Axial_DIN0207_L63mm_D25mm_P762mm_Horizontal_96b38c16849e_ln_024  label="R402_R_Axial_DIN0207_L63mm_D25mm_P762mm_Horizontal_47cc05b15c1c"
  LinkPlacement = pos=(19.812,49.022,0) rot=(0,0,1;0rad)
  LinkedObject = -> Shape005
  Placement = pos=(19.812,49.022,0) rot=(0,0,1;0rad)
FEATURE [App::Link] U403_OPA347PA010_c6fd33d6b5eb_ln_002  label="U402_OPA347PA010_bf3c42dcce77"
  LinkPlacement = pos=(36.83,60.452,0) rot=(0,0,1;0rad)
  LinkedObject = -> OPA347PA010
  Placement = pos=(36.83,60.452,0) rot=(0,0,1;0rad)
FEATURE [App::Link] R424_Potentiometer_Bourns_3296W_Vertical_5014a80db3f9_ln_  label="R420_Potentiometer_Bourns_3296W_Vertical_7ce6f298ed42"
  LinkPlacement = pos=(37.094,20.066,0) rot=(0,0,1;0rad)
  LinkedObject = -> Shape008
  Placement = pos=(37.094,20.066,0) rot=(0,0,1;0rad)
FEATURE [App::Link] R426_R_Axial_DIN0207_L63mm_D25mm_P762mm_Horizontal_96b38c16849e_ln_025  label="R418_R_Axial_DIN0207_L63mm_D25mm_P762mm_Horizontal_928039f00f5f"
  LinkPlacement = pos=(19.558,28.194,0) rot=(0,0,1;0rad)
  LinkedObject = -> Shape005
  Placement = pos=(19.558,28.194,0) rot=(0,0,1;0rad)
FEATURE [App::Part] Top_758f
  Group = -> [Shape005,D_DO_35_SOD27_P7_62mm_Horizontal,R426_R_Axial_DIN0207_L63mm_D25mm_P762mm_Horizontal_96b38c16849e_ln_,Shape006,R426_R_Axial_DIN0207_L63mm_D25mm_P762mm_Horizontal_96b38c16849e_ln_001,R426_R_Axial_DIN0207_L63mm_D25mm_P762mm_Horizontal_96b38c16849e_ln_002,R426_R_Axial_DIN0207_L63mm_D25mm_P762mm_Horizontal_96b38c16849e_ln_003,+44 more]
  Origin = -> Origin018
FEATURE [App::Part] Step_Models_758f
  Group = -> [Top_758f]
  Origin = -> Origin017
FEATURE [App::Part] Board_758f  label="timebase"
  Group = -> [Local_CS_758f,Board_Geoms_758f,Step_Models_758f]
  Origin = -> Origin016
  Placement = pos=(70,-66,102) rot=(1,0,0;4.71239rad)
FEATURE [Part::Feature] Part__Feature060  label="1444-14103"
  Placement = pos=(0,-77.4954,-1.78e-14) rot=(0.57735,0.57735,0.57735;4.18879rad)
  shape: bbox 355.6 x 76.2 x 254 mm, 114 faces (baked)
FEATURE [Part::Feature] Part__Feature061  label="1434-1410"
  shape: bbox 355.6 x 1.295 x 254 mm, 26 faces (baked)
FEATURE [Part::Feature] Part__Feature062  label="6-32 (SC18394)004"
  Placement = pos=(172.263,-1.524,101.6) rot=(0,0,1;0rad)
  shape: bbox 7.29 x 8.224 x 7.29 mm, 27 faces (baked)
FEATURE [Part::Feature] Part__Feature063  label="6-32 (SC18394)005"
  Placement = pos=(-172.263,-1.524,101.6) rot=(0,0,1;0rad)
  shape: bbox 7.29 x 8.224 x 7.29 mm, 27 faces (baked)
FEATURE [Part::Feature] Part__Feature064  label="6-32 (SC18394)006"
  Placement = pos=(-172.263,-1.524,-101.6) rot=(0,0,1;0rad)
  shape: bbox 7.29 x 8.224 x 7.29 mm, 27 faces (baked)
FEATURE [Part::Feature] Part__Feature065  label="6-32 (SC18394)007"
  Placement = pos=(172.263,-1.524,-101.6) rot=(0,0,1;0rad)
  shape: bbox 7.29 x 8.224 x 7.29 mm, 27 faces (baked)
FEATURE [App::Part] _444_14103  label="1444-14104"
  Group = -> [Part__Feature060,Part__Feature061,Part__Feature062,Part__Feature063,Part__Feature064,Part__Feature065]
  Origin = -> Origin027
